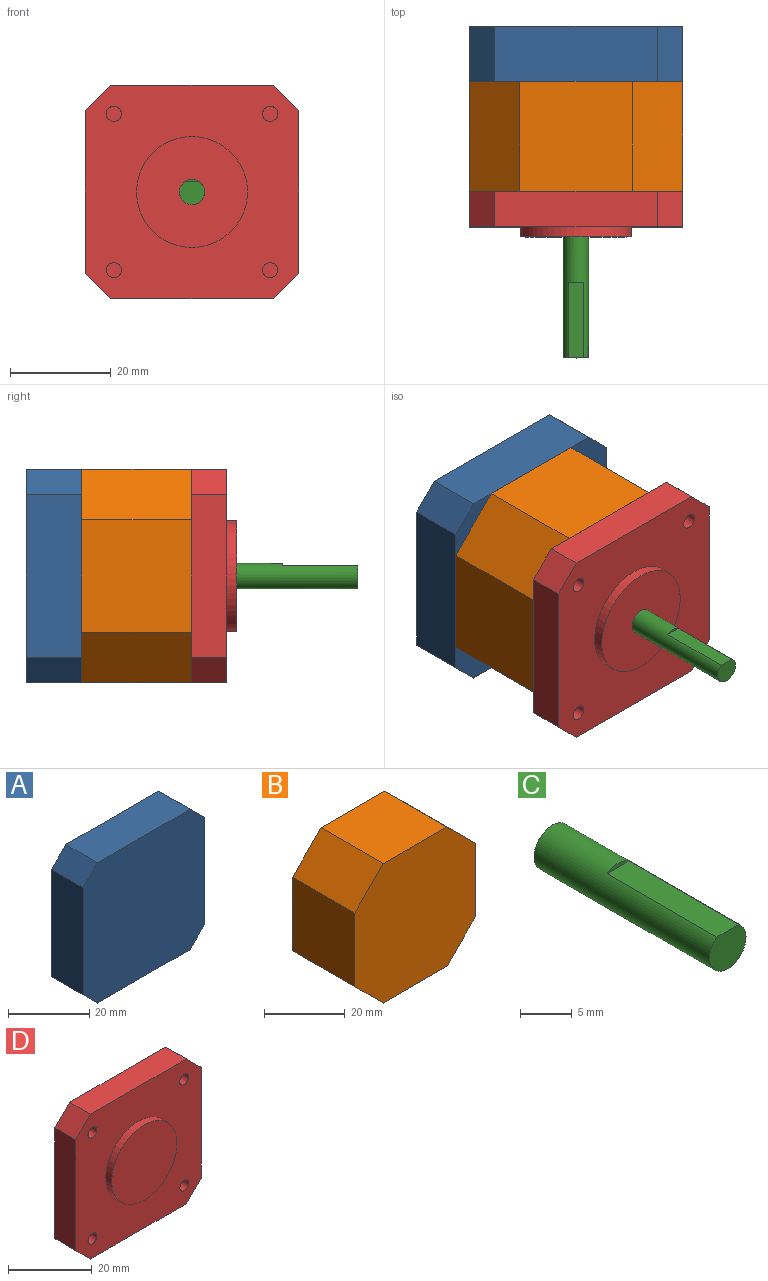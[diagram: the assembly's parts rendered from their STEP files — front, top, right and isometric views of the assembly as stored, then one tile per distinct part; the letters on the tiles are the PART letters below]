
ASSEMBLY  parts=4 mates=3
PART A: 18 faces, bbox 42.3x11x42.3 mm
  f0: plane 32.3x11mm, normal (1,0,0), area 355.3mm2, adj f4,f5,f8,f9
  f1: plane 32.3x11mm, normal (0,0,-1), area 355.3mm2, adj f4,f5,f7,f8
  f2: plane 32.3x11mm, normal (-1,0,0), area 355.3mm2, adj f4,f5,f6,f7
  f3: plane 32.3x11mm, normal (0,0,1), area 355.3mm2, adj f4,f5,f6,f9
  f4: plane 42.3x42.3mm, normal (0,1,0), area 1711mm2, adj f0,f1,f2,f3,f6,f7,f8,f9
  f5: plane 42.3x42.3mm, normal (0,-1,0), area 1739.3mm2, adj f0,f1,f2,f3,f6,f7,f8,f9
  f6: plane 11x5mm, normal (-0.71,0,0.71), area 77.8mm2, adj f2,f3,f4,f5
  f7: plane 11x5mm, normal (-0.71,0,-0.71), area 77.8mm2, adj f1,f2,f4,f5
  f8: plane 11x5mm, normal (0.71,0,-0.71), area 77.8mm2, adj f0,f1,f4,f5
  f9: plane 11x5mm, normal (0.71,0,0.71), area 77.8mm2, adj f0,f3,f4,f5
  f10: cylinder r=1.5mm len=4.5mm, axis (0,1,0), area 42.4mm2, adj f4,f11
  f11: plane 3x3mm, normal (0,1,0), area 7.1mm2, adj f10
  f12: cylinder r=1.5mm len=4.5mm, axis (0,1,0), area 42.4mm2, adj f4,f13
  f13: plane 3x3mm, normal (0,1,0), area 7.1mm2, adj f12
  f14: cylinder r=1.5mm len=4.5mm, axis (0,1,0), area 42.4mm2, adj f4,f15
  f15: plane 3x3mm, normal (0,1,0), area 7.1mm2, adj f14
  f16: cylinder r=1.5mm len=4.5mm, axis (0,1,0), area 42.4mm2, adj f4,f17
  f17: plane 3x3mm, normal (0,1,0), area 7.1mm2, adj f16
PART B: 10 faces, bbox 42.3x21.8x42.3 mm
  f0: plane 21.8x10mm, normal (0.71,0,0.71), area 308.3mm2, adj f3,f6,f7,f8
  f1: plane 21.8x10mm, normal (0.71,0,-0.71), area 308.3mm2, adj f3,f4,f6,f7
  f2: plane 21.8x10mm, normal (-0.71,0,0.71), area 308.3mm2, adj f6,f7,f8,f9
  f3: plane 22.3x21.8mm, normal (1,0,0), area 486.1mm2, adj f0,f1,f6,f7
  f4: plane 22.3x21.8mm, normal (0,0,-1), area 486.1mm2, adj f1,f5,f6,f7
  f5: plane 21.8x10mm, normal (-0.71,0,-0.71), area 308.3mm2, adj f4,f6,f7,f9
  f6: plane 42.3x42.3mm, normal (0,-1,0), area 1589.3mm2, adj f0,f1,f2,f3,f4,f5,f8,f9
  f7: plane 42.3x42.3mm, normal (0,1,0), area 1589.3mm2, adj f0,f1,f2,f3,f4,f5,f8,f9
  f8: plane 22.3x21.8mm, normal (0,0,1), area 486.1mm2, adj f0,f2,f6,f7
  f9: plane 22.3x21.8mm, normal (-1,0,0), area 486.1mm2, adj f2,f5,f6,f7
PART C: 5 faces, bbox 5x24x5 mm
  f0: cylinder r=2.5mm len=24mm, axis (0,1,0), area 328.7mm2, adj f1,f2,f3,f4
  f1: plane 5x4.5mm, normal (0,-1,0), area 18.6mm2, adj f0,f3
  f2: plane 5x5mm, normal (0,1,0), area 19.6mm2, adj f0
  f3: plane 15x3mm, normal (0,0,1), area 45mm2, adj f0,f1,f4
  f4: plane 3x0.5mm, normal (0,-1,0), area 1mm2, adj f0,f3
PART D: 20 faces, bbox 42.3x9x42.3 mm
  f0: plane 42.3x42.3mm, normal (0,-1,0), area 1330.9mm2, adj f1,f2,f3,f4,f6,f7,f8,f9
  f1: plane 32.3x7mm, normal (-1,0,0), area 226.1mm2, adj f0,f5,f6,f9
  f2: plane 32.3x7mm, normal (0,0,-1), area 226.1mm2, adj f0,f5,f6,f7
  f3: plane 32.3x7mm, normal (1,0,0), area 226.1mm2, adj f0,f5,f7,f8
  f4: plane 32.3x7mm, normal (0,0,1), area 226.1mm2, adj f0,f5,f8,f9
  f5: plane 42.3x42.3mm, normal (0,1,0), area 1739.3mm2, adj f1,f2,f3,f4,f6,f7,f8,f9
  f6: plane 7x5mm, normal (-0.71,0,-0.71), area 49.5mm2, adj f0,f1,f2,f5
  f7: plane 7x5mm, normal (0.71,0,-0.71), area 49.5mm2, adj f0,f2,f3,f5
  f8: plane 7x5mm, normal (0.71,0,0.71), area 49.5mm2, adj f0,f3,f4,f5
  f9: plane 7x5mm, normal (-0.71,0,0.71), area 49.5mm2, adj f0,f1,f4,f5
  f10: cylinder r=11mm len=22mm, axis (0,1,0), area 138.2mm2, adj f0,f11
  f11: plane 22x22mm, normal (0,-1,0), area 380.1mm2, adj f10
  f12: cylinder r=1.5mm len=4.5mm, axis (0,-1,0), area 42.4mm2, adj f0,f13
  f13: plane 3x3mm, normal (0,-1,0), area 7.1mm2, adj f12
  f14: cylinder r=1.5mm len=4.5mm, axis (0,-1,0), area 42.4mm2, adj f0,f15
  f15: plane 3x3mm, normal (0,-1,0), area 7.1mm2, adj f14
  f16: cylinder r=1.5mm len=4.5mm, axis (0,-1,0), area 42.4mm2, adj f0,f17
  f17: plane 3x3mm, normal (0,-1,0), area 7.1mm2, adj f16
  f18: cylinder r=1.5mm len=4.5mm, axis (0,-1,0), area 42.4mm2, adj f0,f19
  f19: plane 3x3mm, normal (0,-1,0), area 7.1mm2, adj f18
PLACE A at identity
PLACE B at identity
PLACE C at identity
PLACE D at identity
MATE fastened A.f5 <-> B.f7  axis (0,-1,0) through (-18.45,21.8,13.43)mm
MATE fastened D.f10 <-> B.f6  axis (0,1,0) through (-18.45,0,13.43)mm
MATE revolute C.f0 <-> D.f10  axis (0,1,0) through (-18.45,-9,13.43)mm
